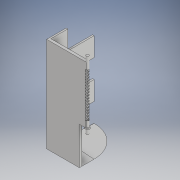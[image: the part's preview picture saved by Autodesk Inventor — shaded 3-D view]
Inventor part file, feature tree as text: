
AUTODESK INVENTOR PART (.ipt)
format: ipt  version: 2018 (Build 220112000, 112)  size: 1,230,848 bytes
history: native  units: mm
features: sketch x12, extrude x12, plane x6, other x3, mirror x2, pattern_circular x1, fillet x1, chamfer x1, projected_geometry x1
ambient origin geometry x8: Origin, YZ Plane, XZ Plane, XY Plane, X Axis, Y Axis, Z Axis, Center Point
bodies: Body1 (feature_tree)
feature tree (39):
  other  "Sólido1"
  sketch  "Boceto1"  dims[d0=100.0mm d1=145.0mm]
  extrude  "Extrusión2"  Depth=145.0mm
  extrude  "Extrusión3"  Depth=4.0mm
  plane  "Plano de trabajo1"
  extrude  "Extrusión4"  Depth=50.0mm TaperAngle=0.0deg
  extrude  "Extrusión5"  Depth=50.0mm TaperAngle=0.0deg
  extrude  "Extrusión6"  Depth=3.0mm
  sketch  "Boceto5"  dims[d29=0.0mm d31=50.0mm d32=0.0mm]
  extrude  "Extrusión8"  Depth=3.0mm
  extrude  "Extrusión9"  Depth=3.0mm
  plane  "Plano de trabajo2"
  other  "Bobina1"
  other  "Eje de trabajo1"
  pattern_circular  "Patrón circular1"  [2 undecoded]
  fillet  "Empalme1"  Radius=2.0mm
  chamfer  "Chaflán4"  Distance=0.5mm
  extrude  "Extrusión10"  Depth=50.0mm TaperAngle=360.0deg
  extrude  "Extrusión11"  Depth=47.5mm
  sketch  "Boceto10"  dims[d50=0.0mm d51=0.0mm]
  plane  "Plano de trabajo4"
  extrude  "Extrusión12"  Depth=2.5mm TaperAngle=45.0deg
  mirror  "Simetría1"
  plane  "Plano de trabajo5"
  plane  "Plano de trabajo6"
  extrude  "Extrusión13"  Depth=4.0mm
  extrude  "Extrusión14"  Depth=10.0mm TaperAngle=0.0deg
  plane  "Plano de trabajo8"
  mirror  "Simetría2"
  sketch  "Boceto2"  dims[d2=4.0mm d12=20.0mm]
  sketch  "Boceto3"  dims[d25=2.5mm d26=0.0mm d27=50.0mm d28=0.0mm]
  projected_geometry  "Contorno proyectado1"
  sketch  "Boceto6"  dims[d33=2.5mm d34=0.0mm d38=3.0mm]
  sketch  "Boceto7"  dims[d42=12.5mm d43=0.0mm d44=3.0mm]
  sketch  "Boceto8"  dims[d45=3.0mm d48=12.5mm]
  sketch  "Boceto9"  dims[d49=12.5mm]
  sketch  "Boceto11"  dims[d52=4.0mm]
  sketch  "Boceto12"  dims[d53=15.0mm d54=0.0mm]
  sketch  "Boceto13"  dims[d56=2.0mm d57=0.5mm d58=2.0mm d59=0.5mm d60=10.0mm d61=100.0mm d62=200.0mm d63=0.0mm d64=90.0deg d65=90.0deg d66=0.0mm d67=0.0mm d68=50.0mm d69=360.0deg d71=47.5mm d75=2.5mm d76=40.0mm d77=45.0deg d78=4.0mm d79=10.0mm d80=0.0mm d81=4.0mm d82=8.0mm d83=0.0mm d85=50.0mm d86=90.0deg d88=1.5mm d89=1.5mm d90=2.499964mm d91=10.0mm d92=0.0mm d98=100.0mm d99=100.0mm d100=4.0mm d101=4.0mm d102=6.0mm d103=2.0mm d104=0.0mm d105=20.0mm d106=29.0mm d107=40.0mm d108=29.0mm d109=40.0mm d110=29.0mm d111=40.0mm d112=29.0mm d113=40.0mm d114=20.0mm d115=29.0mm d116=40.0mm d117=29.0mm d118=40.0mm d119=29.0mm d120=29.0mm d121=10.0mm d122=0.0mm]
note: 2 required parameter values undecoded (feature->parameter linkage not recoverable at this tier; creation-order binding heuristic only, values carry confidence <= 0.55)
